# Revit family: FLAKE-AQ015xxFWSxx0DPO0xxx
name_source: partatom
category: Leuchten
units: mm (PartAtom-declared; Revit-internal decimal feet)

## family parameters
Basisbauteil = Fläche
Beim Laden mit Abzugskörper schneiden = Nein
Bemaßung runder Anschluss = Durchmesser verwenden
Gemeinsam genutzt = Nein
Lichtquelle = Ja
OmniClass-Nummer = 23.80.70.11
OmniClass-Titel = Luminaries for Internal Lighting
Raumberechnungspunkt = Nein
Teiletyp = Normal

## types (6) — shared parameters
Baugruppenkennzeichen = D5020200
Datei für fotometrisches Netz = FLAKE-AQ015.IES
Emissionsform beim Rendern sichtbar = Nein
Farbfilter = 16777215
Farbtemperaturverschiebung bei Dämpfen der Lampe = <Keine Auswahl>
Hersteller = RIDI Leuchten GmbH
Lampe = LED
Neigungswinkel = 90.00°
URL = www.ridi.de
Von Breite des Rechtecks ausssenden = 133 mm  [stored 0.436352 ft]
Von Länge des Rechtecks aussenden = 133 mm  [stored 0.436352 ft]
brand = RIDI
conformity mark = CE
electrical safety class = 1
height = 51 mm
ingress protection (IP) code = IP20
length = 150 mm
nominal frequency = 50-60Hz
nominal voltage = 230
voltage type (AC, DC, UC) = AC
weight = 0.7
width = 150 mm
zero-valued in all types: Vorgabe-Ansicht

## per-type parameters (varying)
| type | Modell | Scheinlast | rated input power |
| FLAKE-AQ015DAFWS830DPO0150 | 0637722AH | 15 VA | 15 |
| FLAKE-AQ015DAFWS840DPO0175 | 0637723AH | 15 VA | 15 |
| FLAKE-AQ015NDFWS830DPO0150 | 0627722AH | 15 VA | 15 |
| FLAKE-AQ015NDFWS840DPO0175 | 0627723AH | 15 VA | 15 |
| FLAKE-AQ015NDFWS830DPO0050 | 0627772AH | 5 VA | 5 |
| FLAKE-AQ015NDFWS840DPO0050 | 0627773AH | 5 VA | 5 |

note: column(s) folded — value = type name in every type: product name

note: [stored X ft] marks values corroborated as IEEE doubles in the binary element streams (Revit-internal decimal feet)
